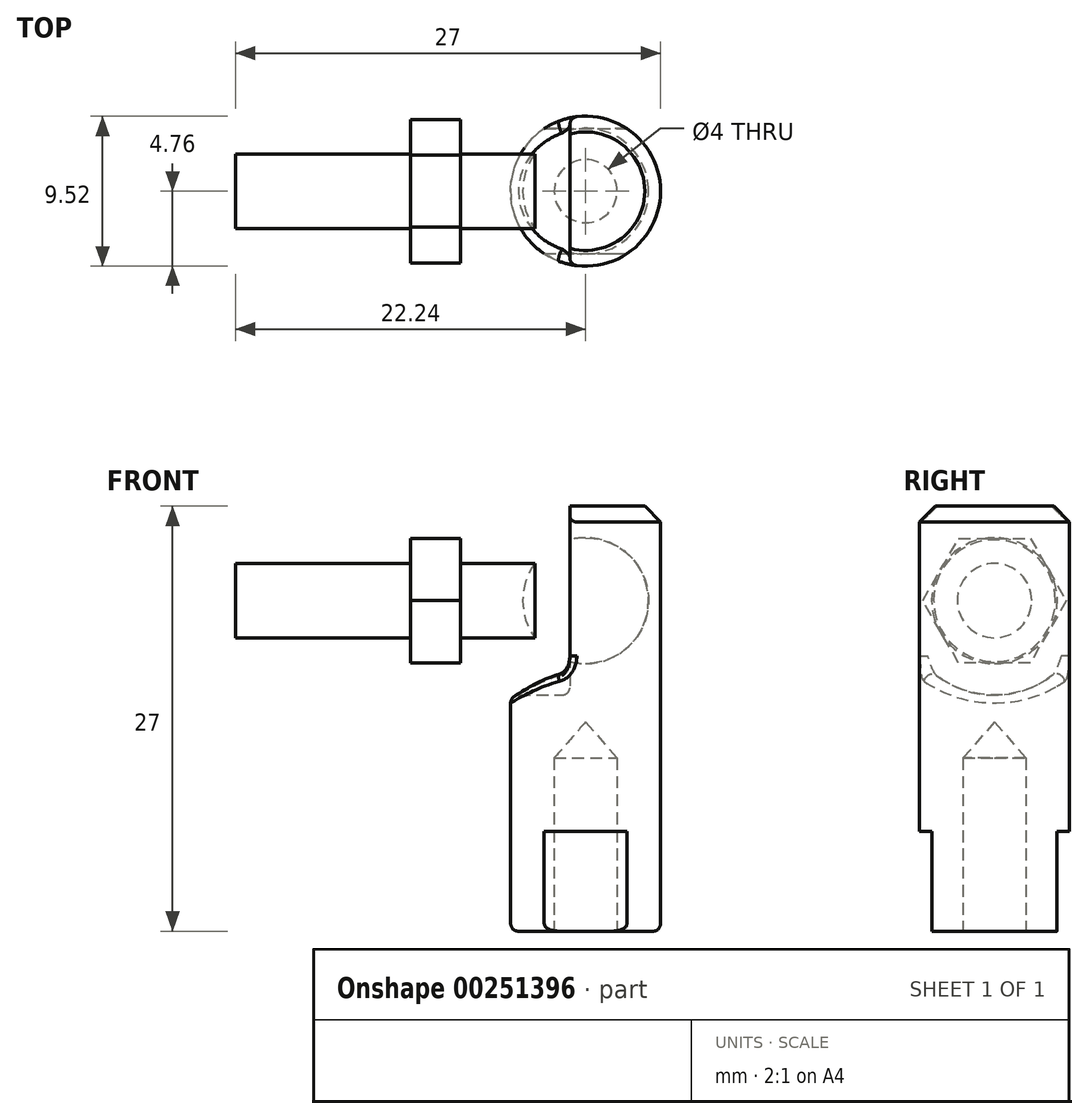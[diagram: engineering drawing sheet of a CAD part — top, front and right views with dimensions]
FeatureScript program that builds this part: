
annotation { "Feature Type Name" : "Feature", "Feature Type Description" : "" }
export const myFeature = defineFeature(function(context is Context, id is Id, definition is map)
    precondition{}
    {
        {
            var Q0;
            Q0=qCreatedBy(makeId("Front.planeOp"),FACE);
            var sketch = newSketch(context, id + "F0", { "sketchPlane" : qUnion([Q0])});
            skLineSegment(sketch, "E0", {"start": v(0, 0) * mm, "end": v(0, 21) * mm, "construction": true});
            skLineSegment(sketch, "E1", {"start": v(0, 21) * mm, "end": v(-22.24, 21) * mm, "construction": true});
            skLineSegment(sketch, "E2", {"start": v(2, 0) * mm, "end": v(4.76, 0) * mm});
            skLineSegment(sketch, "E3", {"start": v(4.76, 0) * mm, "end": v(4.76, 26) * mm});
            skLineSegment(sketch, "E4", {"start": v(3.76, 27) * mm, "end": v(0, 27) * mm});
            skLineSegment(sketch, "E5", {"start": v(0, 27) * mm, "end": v(0, 13.3) * mm});
            skLineSegment(sketch, "E6", {"start": v(2, 0) * mm, "end": v(2, 11) * mm});
            skLineSegment(sketch, "E7", {"start": v(2, 11) * mm, "end": v(0, 13.3) * mm});
            skLineSegment(sketch, "E8", {"start": v(3.76, 27) * mm, "end": v(4.76, 26) * mm});
            skSolve(sketch);
        }
        {
            var Q0;
            Q0 = qSketchRegion(id + "F0", true);
            var Q1;
            Q1=sQuery(id+"F0.wireOp",EDGE,"E0");
            revolve(context, id + "F1", {"entities" : qUnion([Q0]), "axis" : qUnion([Q1]), "revolveType" : RevolveType.FULL});
        }
        {
            var Q0;
            Q0=qCreatedBy(makeId("Right.planeOp"),FACE);
            cPlane(context, id + "F2", {"entities" : qUnion([Q0]), "cplaneType" : CPlaneType.OFFSET, "offset" : 1 * mm, "oppositeDirection" : true, "width" : 152.4 * mm, "height" : 152.4 * mm});
        }
        {
            var Q0;
            Q0=qCreatedBy(id+"F2.planeOp",FACE);
            var sketch = newSketch(context, id + "F3", { "sketchPlane" : qUnion([Q0])});
            skArc(sketch, "E9", {"start": v(6, 21) * mm, "mid": v(0, 15) * mm, "end": v(-6, 21) * mm});
            skLineSegment(sketch, "E10", {"start": v(6, 21) * mm, "end": v(6, 33.35) * mm});
            skLineSegment(sketch, "E11", {"start": v(-6, 33.35) * mm, "end": v(6, 33.35) * mm});
            skLineSegment(sketch, "E12", {"start": v(-6, 33.35) * mm, "end": v(-6, 21) * mm});
            skSolve(sketch);
        }
        {
            var Q0;
            Q0 = qSketchRegion(id + "F3", true);
            extrude(context, id + "F4", {"entities" : qUnion([Q0]), "operationType" : NewBodyOperationType.REMOVE, "oppositeDirection" : true, "depth" : 25.4 * mm});
        }
        {
            var Q0;
            Q0=qCreatedBy(makeId("Front.planeOp"),FACE);
            var sketch = newSketch(context, id + "F5", { "sketchPlane" : qUnion([Q0])});
            skLineSegment(sketch, "E13", {"start": v(0, 21) * mm, "end": v(-22.24, 21) * mm, "construction": true});
            skLineSegment(sketch, "E14", {"start": v(-22.24, 21) * mm, "end": v(-22.24, 23.36) * mm});
            skLineSegment(sketch, "E15", {"start": v(-22.24, 23.36) * mm, "end": v(-11.12, 23.36) * mm});
            skLineSegment(sketch, "E16", {"start": v(-11.12, 23.36) * mm, "end": v(-11.12, 24.95) * mm});
            skLineSegment(sketch, "E17", {"start": v(-11.12, 24.95) * mm, "end": v(-7.95, 24.95) * mm});
            skLineSegment(sketch, "E18", {"start": v(-7.95, 24.95) * mm, "end": v(-7.95, 23.36) * mm});
            skLineSegment(sketch, "E19", {"start": v(-7.95, 23.36) * mm, "end": v(-3.19, 23.36) * mm});
            skArc(sketch, "E20", {"start": v(3.97, 21) * mm, "mid": v(1.24, 24.77) * mm, "end": v(-3.19, 23.36) * mm});
            skLineSegment(sketch, "E21", {"start": v(3.97, 21) * mm, "end": v(-22.24, 21) * mm});
            skSolve(sketch);
        }
        {
            var Q0;
            Q0=makeQuery(id+"F5.imprint","IMPRINT",FACE,{"disambiguationData":[TD([[makeQuery(id+"F5.imprint","IMPRINT",EDGE,{"derivedFrom":sQuery(id+"F5.wireOp",EDGE,"E14")}),-1.0]])]});
            var Q1;
            Q1=sQuery(id+"F5.wireOp",EDGE,"E21");
            revolve(context, id + "F6", {"entities" : qUnion([Q0]), "axis" : qUnion([Q1]), "revolveType" : RevolveType.FULL});
        }
        {
            var Q0;
            Q0=makeQuery(id+"F6.opRevolve","SWEPT_FACE",FACE,{"disambiguationData":[OSD([sQuery(id+"F5.wireOp",EDGE,"E16")])]});
            var sketch = newSketch(context, id + "F7", { "sketchPlane" : qUnion([Q0])});
            skCircle(sketch, "E22.cCircle", {"center": v(0, 21) * mm, "radius": 3.95 * mm, "construction": true});
            skLineSegment(sketch, "E22.0", {"start": v(-2.28, 24.95) * mm, "end": v(2.28, 24.95) * mm});
            skLineSegment(sketch, "E22.1", {"start": v(2.28, 24.95) * mm, "end": v(4.56, 21) * mm});
            skLineSegment(sketch, "E22.2", {"start": v(4.56, 21) * mm, "end": v(2.28, 17.05) * mm});
            skLineSegment(sketch, "E22.3", {"start": v(2.28, 17.05) * mm, "end": v(-2.28, 17.05) * mm});
            skLineSegment(sketch, "E22.4", {"start": v(-2.28, 17.05) * mm, "end": v(-4.56, 21) * mm});
            skLineSegment(sketch, "E22.5", {"start": v(-4.56, 21) * mm, "end": v(-2.28, 24.95) * mm});
            skPoint(sketch, "E22.0.midPoint", {"position": v(0, 24.95) * mm});
            skSolve(sketch);
        }
        {
            var Q0;
            Q0 = qSketchRegion(id + "F7", true);
            var Q1;
            Q1=makeQuery(id+"F6.opRevolve","SWEPT_FACE",FACE,{"disambiguationData":[OSD([sQuery(id+"F5.wireOp",EDGE,"E18")])]});
            extrude(context, id + "F8", {"entities" : qUnion([Q0]), "operationType" : NewBodyOperationType.ADD, "endBound" : BoundingType.UP_TO_SURFACE, "oppositeDirection" : true, "endBoundEntityFace" : qUnion([Q1]), "depth" : 25.4 * mm});
        }
        {
            var Q0;
            Q0=qCreatedBy(makeId("Right.planeOp"),FACE);
            var sketch = newSketch(context, id + "F9", { "sketchPlane" : qUnion([Q0])});
            skLineSegment(sketch, "E23", {"start": v(0, 0) * mm, "end": v(0, 29.5) * mm, "construction": true});
            skLineSegment(sketch, "E24.bottom", {"start": v(-3.97, 0) * mm, "end": v(-6.35, 0) * mm});
            skLineSegment(sketch, "E24.top", {"start": v(-3.97, 6.35) * mm, "end": v(-6.35, 6.35) * mm});
            skLineSegment(sketch, "E24.left", {"start": v(-3.97, 0) * mm, "end": v(-3.97, 6.35) * mm});
            skLineSegment(sketch, "E24.right", {"start": v(-6.35, 0) * mm, "end": v(-6.35, 6.35) * mm});
            skLineSegment(sketch, "E25.MirrorCS", {"start": v(3.97, 0) * mm, "end": v(6.35, 0) * mm});
            skLineSegment(sketch, "E26.MirrorCS", {"start": v(3.97, 6.35) * mm, "end": v(6.35, 6.35) * mm});
            skLineSegment(sketch, "E27.MirrorCS", {"start": v(3.97, 0) * mm, "end": v(3.97, 6.35) * mm});
            skLineSegment(sketch, "E28.MirrorCS", {"start": v(6.35, 0) * mm, "end": v(6.35, 6.35) * mm});
            skSolve(sketch);
        }
        {
            var Q0;
            Q0 = qSketchRegion(id + "F9", true);
            extrude(context, id + "F10", {"entities" : qUnion([Q0]), "operationType" : NewBodyOperationType.REMOVE, "endBound" : BoundingType.THROUGH_ALL, "oppositeDirection" : true, "depth" : 25.4 * mm, "hasSecondDirection" : true, "secondDirectionBound" : BoundingType.THROUGH_ALL, "secondDirectionOppositeDirection" : false, "secondDirectionDepth" : 25.4 * mm});
        }
        {
            var Q0;
            Q0=makeQuery(id+"F4.boolean.opBoolean","COPY",EDGE,{"derivedFrom":makeQuery(id+"F4.opExtrude","CAP_EDGE",EDGE,{"disambiguationData":[OSD([sQuery(id+"F3.wireOp",EDGE,"E9")])],"isStart":true})});
            var Q1;
            Q1=makeQuery(id+"F10.boolean.opBoolean","SPLIT",EDGE,{"disambiguationData":[OD(0.0)],"derivedFrom":makeQuery(id+"F1.opRevolve","SWEPT_EDGE",EDGE,{"disambiguationData":[OSD([sQuery(id+"F0.wireOp",EDGE,"E2"),sQuery(id+"F0.wireOp",EDGE,"E3")])]})});
            var Q2;
            Q2=makeQuery(id+"F10.boolean.opBoolean","SPLIT",EDGE,{"disambiguationData":[OD(1.0)],"derivedFrom":makeQuery(id+"F1.opRevolve","SWEPT_EDGE",EDGE,{"disambiguationData":[OSD([sQuery(id+"F0.wireOp",EDGE,"E2"),sQuery(id+"F0.wireOp",EDGE,"E3")])]})});
            fillet(context, id + "F11", {"entities" : qUnion([Q0, Q1, Q2]), "radius" : .5 * mm, "tangentPropagation" : true, "allowEdgeOverflow" : false});
        }
        {
            var Q0;
            Q0=makeQuery(id+"F4.boolean.opBoolean","INTERSECT",EDGE,{"derivedFrom":[makeQuery(id+"F1.opRevolve","SWEPT_FACE",FACE,{"disambiguationData":[OSD([sQuery(id+"F0.wireOp",EDGE,"E3")])]}),makeQuery(id+"F4.opExtrude","SWEPT_FACE",FACE,{"disambiguationData":[OSD([sQuery(id+"F3.wireOp",EDGE,"E9")])]})]});
            fillet(context, id + "F12", {"entities" : qUnion([Q0]), "radius" : .5 * mm, "tangentPropagation" : true, "allowEdgeOverflow" : false});
        }
        {
            var Q0;
            Q0=qCreatedBy(makeId("Front.planeOp"),FACE);
            var sketch = newSketch(context, id + "F13", { "sketchPlane" : qUnion([Q0])});
            skLineSegment(sketch, "E29", {"start": v(0, 25) * mm, "end": v(0, 17) * mm});
            skArc(sketch, "E30", {"start": v(0, 17) * mm, "mid": v(4, 21) * mm, "end": v(0, 25) * mm});
            skSolve(sketch);
        }
        {
            var Q0;
            Q0 = qSketchRegion(id + "F13", true);
            var Q1;
            Q1=sQuery(id+"F13.wireOp",EDGE,"E29");
            revolve(context, id + "F14", {"operationType" : NewBodyOperationType.REMOVE, "entities" : qUnion([Q0]), "axis" : qUnion([Q1]), "revolveType" : RevolveType.FULL, "oppositeDirection" : true});
        }
    });
